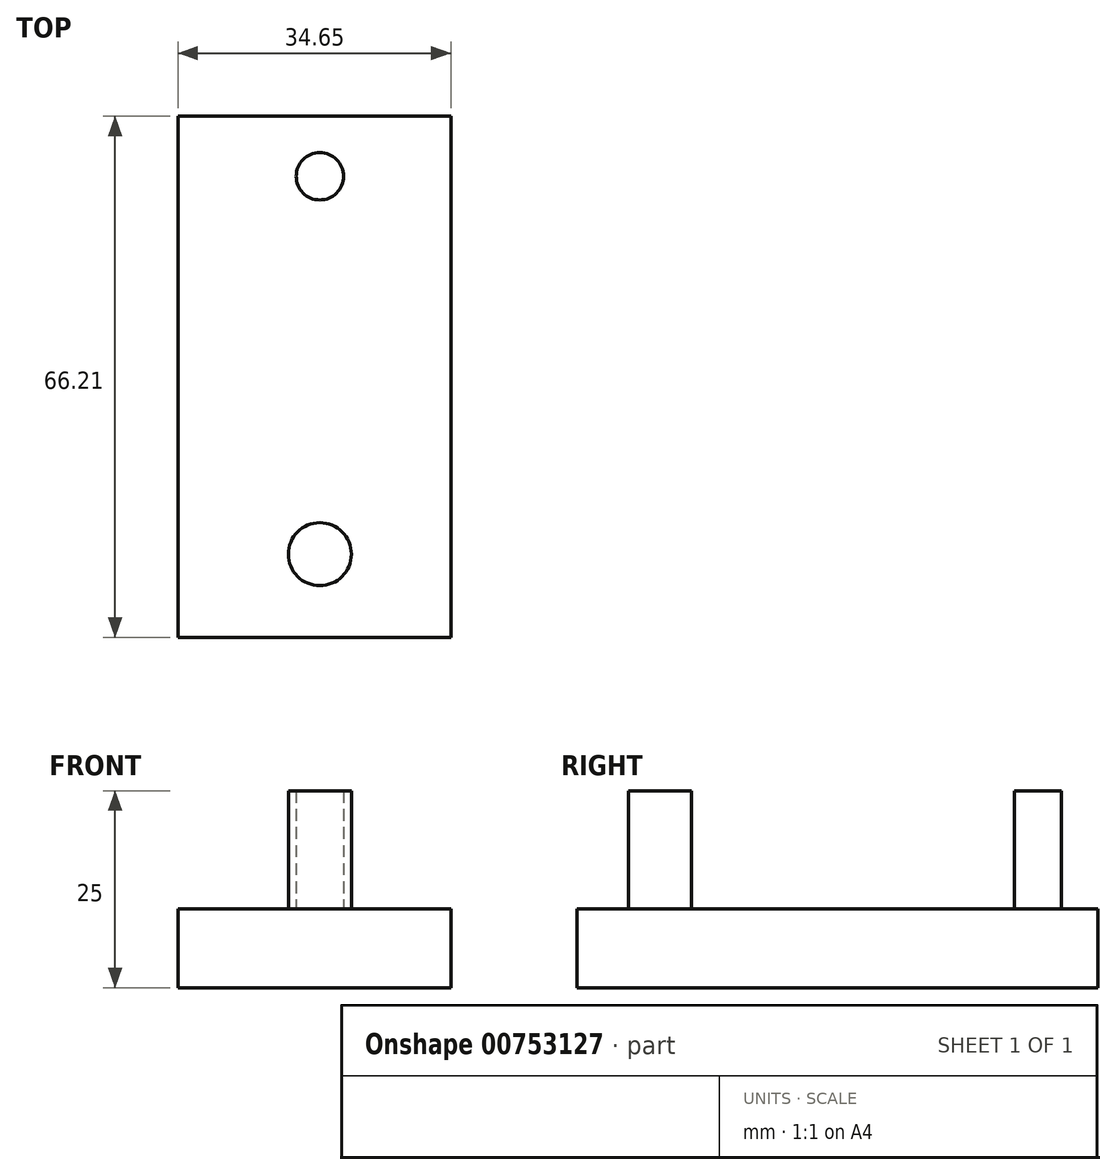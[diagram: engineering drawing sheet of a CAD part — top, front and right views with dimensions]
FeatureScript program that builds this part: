
annotation { "Feature Type Name" : "Feature", "Feature Type Description" : "" }
export const myFeature = defineFeature(function(context is Context, id is Id, definition is map)
    precondition{}
    {
        {
            var Q0;
            Q0=qCreatedBy(makeId("Top.planeOp"),FACE);
            var sketch = newSketch(context, id + "F0", { "sketchPlane" : qUnion([Q0])});
            skCircle(sketch, "E0", {"center": v(0, 33.2) * mm, "radius": 3 * mm});
            skCircle(sketch, "E1", {"center": v(0, -14.8) * mm, "radius": 4 * mm});
            skLineSegment(sketch, "E2.bottom", {"start": v(-18, 40.83) * mm, "end": v(16.65, 40.83) * mm});
            skLineSegment(sketch, "E2.top", {"start": v(-18, -25.38) * mm, "end": v(16.65, -25.38) * mm});
            skLineSegment(sketch, "E2.left", {"start": v(-18, 40.83) * mm, "end": v(-18, -25.38) * mm});
            skLineSegment(sketch, "E2.right", {"start": v(16.65, 40.83) * mm, "end": v(16.65, -25.38) * mm});
            skSolve(sketch);
        }
        {
            var Q0;
            Q0=makeQuery(id+"F0.imprint","IMPRINT",FACE,{"disambiguationData":[TD([[makeQuery(id+"F0.imprint","IMPRINT",EDGE,{"derivedFrom":sQuery(id+"F0.wireOp",EDGE,"E0")}),1.0]])]});
            var Q1;
            Q1=makeQuery(id+"F0.imprint","IMPRINT",FACE,{"disambiguationData":[TD([[makeQuery(id+"F0.imprint","IMPRINT",EDGE,{"derivedFrom":sQuery(id+"F0.wireOp",EDGE,"E1")}),1.0]])]});
            var Q2;
            Q2=makeQuery(id+"F0.imprint","IMPRINT",FACE,{"disambiguationData":[TD([[makeQuery(id+"F0.imprint","IMPRINT",EDGE,{"derivedFrom":sQuery(id+"F0.wireOp",EDGE,"E0")}),-1.0]])]});
            extrude(context, id + "F1", {"entities" : qUnion([Q0, Q1, Q2]), "depth" : 10 * mm, "offsetDistance" : 25 * mm});
        }
        {
            var Q0;
            Q0=makeQuery(id+"F0.imprint","IMPRINT",FACE,{"disambiguationData":[TD([[makeQuery(id+"F0.imprint","IMPRINT",EDGE,{"derivedFrom":sQuery(id+"F0.wireOp",EDGE,"E1")}),1.0]])]});
            var Q1;
            Q1=makeQuery(id+"F0.imprint","IMPRINT",FACE,{"disambiguationData":[TD([[makeQuery(id+"F0.imprint","IMPRINT",EDGE,{"derivedFrom":sQuery(id+"F0.wireOp",EDGE,"E0")}),1.0]])]});
            extrude(context, id + "F2", {"entities" : qUnion([Q0, Q1]), "operationType" : NewBodyOperationType.ADD, "depth" : 25 * mm, "offsetDistance" : 25 * mm});
        }
    });
